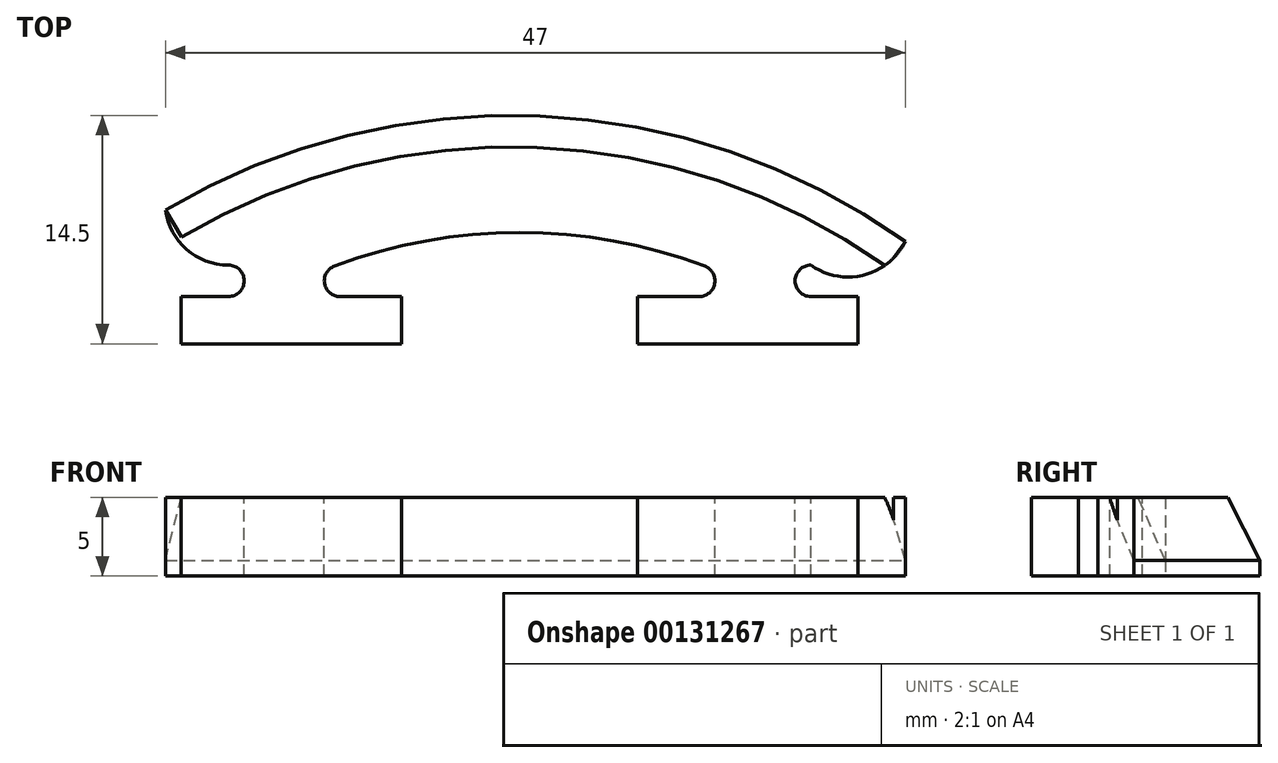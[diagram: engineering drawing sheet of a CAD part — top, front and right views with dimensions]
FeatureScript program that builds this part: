
annotation { "Feature Type Name" : "Feature", "Feature Type Description" : "" }
export const myFeature = defineFeature(function(context is Context, id is Id, definition is map)
    precondition{}
    {
        {
            var Q0;
            Q0=qCreatedBy(makeId("Top.planeOp"),FACE);
            var sketch = newSketch(context, id + "F0", { "sketchPlane" : qUnion([Q0])});
            skLineSegment(sketch, "E0", {"start": v(-23.5, 0) * mm, "end": v(23.5, 0) * mm});
            skLineSegment(sketch, "E1", {"start": v(-23.5, 0) * mm, "end": v(-23.5, 8.5) * mm});
            skLineSegment(sketch, "E2", {"start": v(23.5, 0) * mm, "end": v(23.5, 6.5) * mm});
            skArc(sketch, "E3", {"start": v(23.5, 6.5) * mm, "mid": v(0.3, 14.46) * mm, "end": v(-23.5, 8.5) * mm});
            skLineSegment(sketch, "E4", {"start": v(-23.5, 14.5) * mm, "end": v(23.5, 14.5) * mm, "construction": true});
            skSolve(sketch);
        }
        {
            var Q0;
            Q0=makeQuery(id+"F0.imprint","IMPRINT",FACE,{"disambiguationData":[TD([[makeQuery(id+"F0.imprint","IMPRINT",EDGE,{"derivedFrom":sQuery(id+"F0.wireOp",EDGE,"E0")}),1.0]])]});
            extrude(context, id + "F1", {"entities" : qUnion([Q0]), "depth" : 5 * mm});
        }
        {
            var Q0;
            Q0=makeQuery(id+"F1.opExtrude","CAP_FACE",FACE,{"disambiguationData":[OSD([sQuery(id+"F0.wireOp",EDGE,"E0"),sQuery(id+"F0.wireOp",EDGE,"E1"),sQuery(id+"F0.wireOp",EDGE,"E2"),sQuery(id+"F0.wireOp",EDGE,"E3")])],"isStart":false});
            var sketch = newSketch(context, id + "F2", { "sketchPlane" : qUnion([Q0])});
            skLineSegment(sketch, "E5", {"start": v(-22.5, 0) * mm, "end": v(-8.5, 0) * mm, "construction": true});
            skLineSegment(sketch, "E6", {"start": v(6.5, 0) * mm, "end": v(20.5, 0) * mm, "construction": true});
            skLineSegment(sketch, "E7", {"start": v(-22.5, 0) * mm, "end": v(-22.5, 3) * mm});
            skLineSegment(sketch, "E8", {"start": v(-8.5, 0) * mm, "end": v(-8.5, 3) * mm});
            skLineSegment(sketch, "E9", {"start": v(6.5, 0) * mm, "end": v(6.5, 3) * mm});
            skLineSegment(sketch, "E10", {"start": v(20.5, 0) * mm, "end": v(20.5, 3) * mm});
            skLineSegment(sketch, "E11", {"start": v(-8.5, 3) * mm, "end": v(-12.4, 3) * mm});
            skLineSegment(sketch, "E12", {"start": v(6.5, 3) * mm, "end": v(10.4, 3) * mm});
            skLineSegment(sketch, "E13", {"start": v(20.5, 3) * mm, "end": v(17.5, 3) * mm});
            skLineSegment(sketch, "E14", {"start": v(-22.5, 3) * mm, "end": v(-19.5, 3) * mm});
            skArc(sketch, "E15", {"start": v(-19.5, 3) * mm, "mid": v(-18.5, 4) * mm, "end": v(-19.5, 5) * mm});
            skArc(sketch, "E16", {"start": v(-23.5, 8.5) * mm, "mid": v(-22.16, 6) * mm, "end": v(-19.5, 5) * mm});
            skArc(sketch, "E17", {"start": v(17.5, 5) * mm, "mid": v(16.5, 4) * mm, "end": v(17.5, 3) * mm});
            skArc(sketch, "E18", {"start": v(17.5, 5) * mm, "mid": v(20.85, 4.36) * mm, "end": v(23.5, 6.5) * mm});
            skArc(sketch, "E19", {"start": v(-12.76, 4.94) * mm, "mid": v(-13.4, 3.82) * mm, "end": v(-12.4, 3) * mm});
            skArc(sketch, "E20", {"start": v(10.4, 3) * mm, "mid": v(11.4, 3.82) * mm, "end": v(10.76, 4.94) * mm});
            skArc(sketch, "E21", {"start": v(10.76, 4.94) * mm, "mid": v(-1, 7.07) * mm, "end": v(-12.76, 4.94) * mm});
            skLineSegment(sketch, "E22", {"start": v(-8.5, 0) * mm, "end": v(6.5, 0) * mm, "construction": true});
            skLineSegment(sketch, "E23", {"start": v(-23.5, 8.5) * mm, "end": v(-23.5, 0) * mm});
            skLineSegment(sketch, "E24", {"start": v(-23.5, 0) * mm, "end": v(-22.5, 0) * mm});
            skLineSegment(sketch, "E25", {"start": v(20.5, 0) * mm, "end": v(23.5, 0) * mm});
            skLineSegment(sketch, "E26", {"start": v(23.5, 0) * mm, "end": v(23.5, 6.5) * mm});
            skSolve(sketch);
        }
        {
            var Q0;
            Q0=makeQuery(id+"F2.imprint","IMPRINT",FACE,{"disambiguationData":[TD([[makeQuery(id+"F2.imprint","IMPRINT",EDGE,{"derivedFrom":sQuery(id+"F2.wireOp",EDGE,"E7")}),1.0]])]});
            var Q1;
            {var subQ1=sQuery(id+"F2.wireOp",EDGE,"E8");Q1=makeQuery(id+"F2.imprint","IMPRINT",FACE,{"disambiguationData":[TD([[makeQuery(id+"F2.imprint","IMPRINT",EDGE,{"derivedFrom":subQ1}),-1.0]])]});}
            var Q2;
            Q2=makeQuery(id+"F2.imprint","IMPRINT",FACE,{"disambiguationData":[TD([[makeQuery(id+"F2.imprint","IMPRINT",EDGE,{"derivedFrom":sQuery(id+"F2.wireOp",EDGE,"E10")}),-1.0]])]});
            extrude(context, id + "F3", {"entities" : qUnion([Q0, Q1, Q2]), "operationType" : NewBodyOperationType.REMOVE, "oppositeDirection" : true, "depth" : 25 * mm});
        }
        {
            var Q0;
            Q0=makeQuery(id+"F1.opExtrude","CAP_EDGE",EDGE,{"disambiguationData":[OSD([sQuery(id+"F0.wireOp",EDGE,"E3")])],"isStart":true});
            var Q1;
            Q1=makeQuery(id+"F1.opExtrude","CAP_VERTEX",VERTEX,{"disambiguationData":[OSD([sQuery(id+"F0.wireOp",EDGE,"E1"),sQuery(id+"F0.wireOp",EDGE,"E3")])],"isStart":true});
            cPlane(context, id + "F4", {"entities" : qUnion([Q0, Q1]), "cplaneType" : CPlaneType.CURVE_POINT, "offset" : 25 * mm, "width" : 150 * mm, "height" : 150 * mm});
        }
        {
            var Q0;
            Q0=qCreatedBy(id+"F4.planeOp",FACE);
            var sketch = newSketch(context, id + "F5", { "sketchPlane" : qUnion([Q0])});
            skLineSegment(sketch, "E27", {"start": v(-17.27, 5) * mm, "end": v(-17.27, 0) * mm, "construction": true});
            skLineSegment(sketch, "E28", {"start": v(-17.27, 0) * mm, "end": v(-19.27, 0) * mm, "construction": true});
            skLineSegment(sketch, "E29", {"start": v(-19.27, 0) * mm, "end": v(-19.27, 1) * mm, "construction": true});
            skLineSegment(sketch, "E30", {"start": v(-19.27, 1) * mm, "end": v(-17.27, 5) * mm});
            skLineSegment(sketch, "E31", {"start": v(-19.27, 1) * mm, "end": v(-19.27, 5) * mm});
            skLineSegment(sketch, "E32", {"start": v(-19.27, 5) * mm, "end": v(-17.27, 5) * mm});
            skSolve(sketch);
        }
        {
            var Q0;
            Q0 = qSketchRegion(id + "F5", true);
            var Q1;
            Q1=makeQuery(id+"F1.opExtrude","CAP_EDGE",EDGE,{"disambiguationData":[OSD([sQuery(id+"F0.wireOp",EDGE,"E3")])],"isStart":true});
            sweep(context, id + "F6", {"operationType" : NewBodyOperationType.REMOVE, "profiles" : qUnion([Q0]), "path" : qUnion([Q1])});
        }
    });
